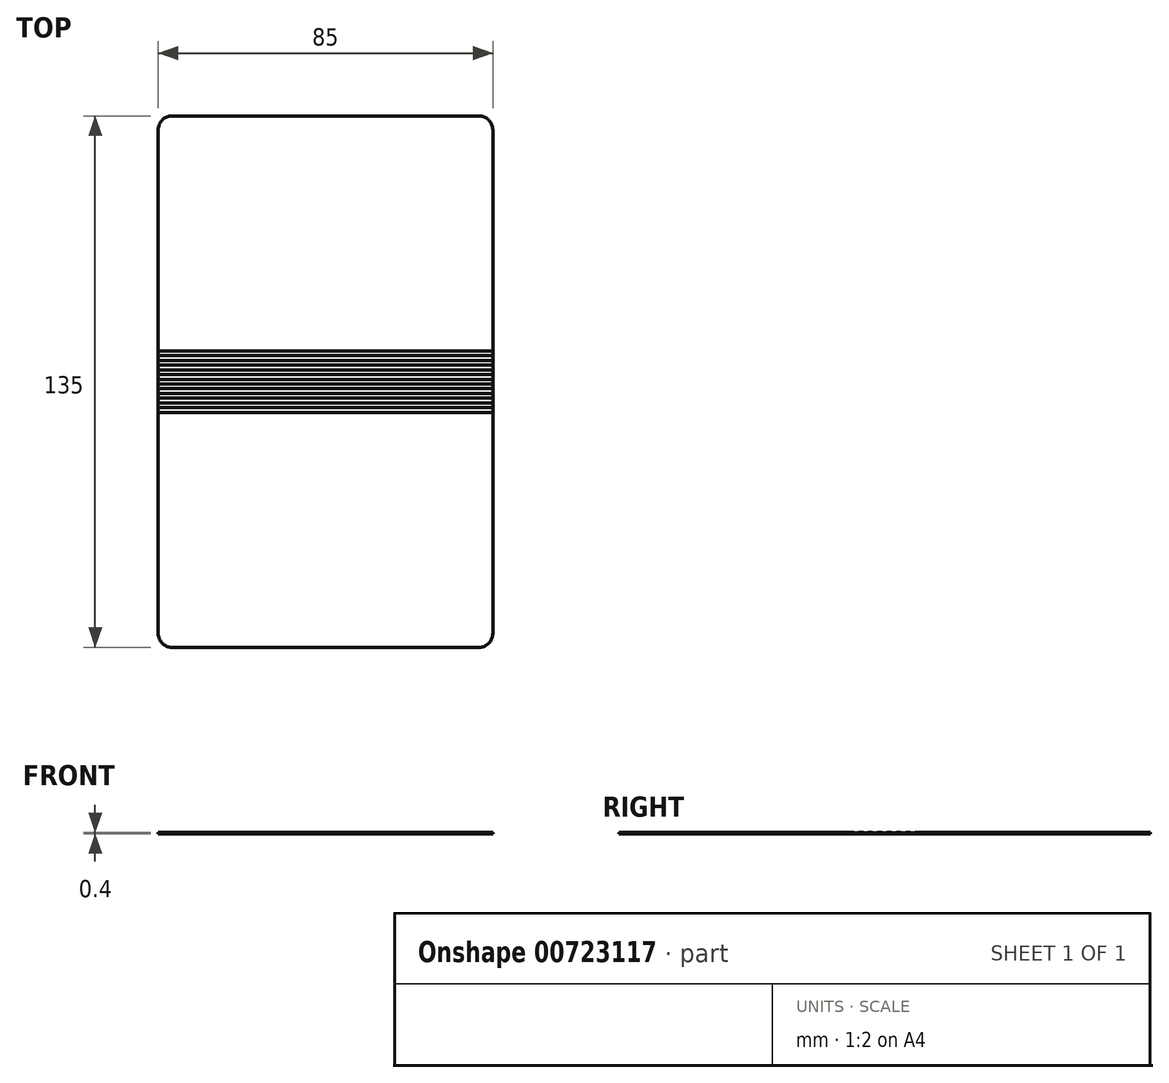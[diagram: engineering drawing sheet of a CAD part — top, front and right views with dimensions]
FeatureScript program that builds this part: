
annotation { "Feature Type Name" : "Feature", "Feature Type Description" : "" }
export const myFeature = defineFeature(function(context is Context, id is Id, definition is map)
    precondition{}
    {
        {
            var Q0;
            Q0=qCreatedBy(makeId("Top.planeOp"),FACE);
            var sketch = newSketch(context, id + "F0", { "sketchPlane" : qUnion([Q0])});
            skLineSegment(sketch, "E0.bottom", {"start": v(39, 67.5) * mm, "end": v(-39, 67.5) * mm});
            skLineSegment(sketch, "E0.top", {"start": v(39, -67.5) * mm, "end": v(-39, -67.5) * mm});
            skLineSegment(sketch, "E0.left", {"start": v(42.5, 64) * mm, "end": v(42.5, -64) * mm});
            skLineSegment(sketch, "E0.right", {"start": v(-42.5, 64) * mm, "end": v(-42.5, -64) * mm});
            skPoint(sketch, "E0.middle", {"position": v(0, 0) * mm});
            skPoint(sketch, "E1.visualSharp", {"position": v(-42.5, 67.5) * mm});
            skArc(sketch, "E1.filletArc", {"start": v(-39, 67.5) * mm, "mid": v(-41.47, 66.47) * mm, "end": v(-42.5, 64) * mm});
            skPoint(sketch, "E2.visualSharp", {"position": v(42.5, 67.5) * mm});
            skArc(sketch, "E2.filletArc", {"start": v(42.5, 64) * mm, "mid": v(41.47, 66.47) * mm, "end": v(39, 67.5) * mm});
            skPoint(sketch, "E3.visualSharp", {"position": v(42.5, -67.5) * mm});
            skArc(sketch, "E3.filletArc", {"start": v(39, -67.5) * mm, "mid": v(41.47, -66.47) * mm, "end": v(42.5, -64) * mm});
            skPoint(sketch, "E4.visualSharp", {"position": v(-42.5, -67.5) * mm});
            skArc(sketch, "E4.filletArc", {"start": v(-42.5, -64) * mm, "mid": v(-41.47, -66.47) * mm, "end": v(-39, -67.5) * mm});
            skSolve(sketch);
        }
        {
            var Q0;
            Q0=qSketchRegion(id+"F0",true);
            extrude(context, id + "F1", {"entities" : qUnion([Q0]), "depth" : .2 * mm, "offsetDistance" : 25 * mm});
        }
        {
            var Q0;
            Q0=makeQuery(id+"F1.opExtrude","CAP_FACE",FACE,{"disambiguationData":[OSD([sQuery(id+"F0.wireOp",EDGE,"E0.bottom"),sQuery(id+"F0.wireOp",EDGE,"E0.top"),sQuery(id+"F0.wireOp",EDGE,"E0.left"),sQuery(id+"F0.wireOp",EDGE,"E0.right"),sQuery(id+"F0.wireOp",EDGE,"E1.filletArc"),sQuery(id+"F0.wireOp",EDGE,"E2.filletArc"),sQuery(id+"F0.wireOp",EDGE,"E3.filletArc"),sQuery(id+"F0.wireOp",EDGE,"E4.filletArc")])],"isStart":false});
            var sketch = newSketch(context, id + "F2", { "sketchPlane" : qUnion([Q0])});
            skLineSegment(sketch, "E5.0", {"start": v(-42.5, -0.6) * mm, "end": v(42.5, -0.6) * mm});
            skLineSegment(sketch, "E6.0", {"start": v(-42.5, 0.6) * mm, "end": v(42.5, 0.6) * mm});
            skLineSegment(sketch, "E7", {"start": v(-42.5, 0.6) * mm, "end": v(-42.5, -0.6) * mm});
            skLineSegment(sketch, "E8", {"start": v(42.5, 0.6) * mm, "end": v(42.5, -0.6) * mm});
            skLineSegment(sketch, "E9.0.1.0", {"start": v(42.5, 3) * mm, "end": v(42.5, 1.8) * mm});
            skLineSegment(sketch, "E9.0.1.1", {"start": v(-42.5, 3) * mm, "end": v(42.5, 3) * mm});
            skLineSegment(sketch, "E9.0.1.2", {"start": v(-42.5, 1.8) * mm, "end": v(42.5, 1.8) * mm});
            skLineSegment(sketch, "E9.0.1.3", {"start": v(-42.5, 3) * mm, "end": v(-42.5, 1.8) * mm});
            skLineSegment(sketch, "E9.0.2.0", {"start": v(42.5, 5.4) * mm, "end": v(42.5, 4.2) * mm});
            skLineSegment(sketch, "E9.0.2.1", {"start": v(-42.5, 5.4) * mm, "end": v(42.5, 5.4) * mm});
            skLineSegment(sketch, "E9.0.2.2", {"start": v(-42.5, 4.2) * mm, "end": v(42.5, 4.2) * mm});
            skLineSegment(sketch, "E9.0.2.3", {"start": v(-42.5, 5.4) * mm, "end": v(-42.5, 4.2) * mm});
            skLineSegment(sketch, "E9.direction1", {"start": v(42.5, -0.6) * mm, "end": v(67.5, -0.6) * mm, "construction": true});
            skLineSegment(sketch, "E9.direction2", {"start": v(42.5, -0.6) * mm, "end": v(42.5, 1.8) * mm, "construction": true});
            skLineSegment(sketch, "E10.MirrorCS", {"start": v(-42.5, -1.8) * mm, "end": v(42.5, -1.8) * mm});
            skLineSegment(sketch, "E11.MirrorCS", {"start": v(42.5, -3) * mm, "end": v(42.5, -1.8) * mm});
            skLineSegment(sketch, "E12.MirrorCS", {"start": v(-42.5, -3) * mm, "end": v(42.5, -3) * mm});
            skLineSegment(sketch, "E13.MirrorCS", {"start": v(-42.5, -4.2) * mm, "end": v(42.5, -4.2) * mm});
            skLineSegment(sketch, "E14.MirrorCS", {"start": v(42.5, -5.4) * mm, "end": v(42.5, -4.2) * mm});
            skLineSegment(sketch, "E15.MirrorCS", {"start": v(-42.5, -5.4) * mm, "end": v(42.5, -5.4) * mm});
            skLineSegment(sketch, "E16.MirrorCS", {"start": v(-42.5, -5.4) * mm, "end": v(-42.5, -4.2) * mm});
            skLineSegment(sketch, "E17.MirrorCS", {"start": v(-42.5, -3) * mm, "end": v(-42.5, -1.8) * mm});
            skLineSegment(sketch, "E18.0.0.3", {"start": v(42.5, 7.8) * mm, "end": v(42.5, 6.6) * mm});
            skLineSegment(sketch, "E18.3.0.3", {"start": v(-42.5, 7.8) * mm, "end": v(42.5, 7.8) * mm});
            skLineSegment(sketch, "E18.6.0.3", {"start": v(-42.5, 6.6) * mm, "end": v(42.5, 6.6) * mm});
            skLineSegment(sketch, "E18.9.0.3", {"start": v(-42.5, 7.8) * mm, "end": v(-42.5, 6.6) * mm});
            skLineSegment(sketch, "E19.MirrorCS", {"start": v(42.5, -7.8) * mm, "end": v(42.5, -6.6) * mm});
            skLineSegment(sketch, "E20.MirrorCS", {"start": v(-42.5, -6.6) * mm, "end": v(42.5, -6.6) * mm});
            skLineSegment(sketch, "E21.MirrorCS", {"start": v(-42.5, -7.8) * mm, "end": v(42.5, -7.8) * mm});
            skLineSegment(sketch, "E22.MirrorCS", {"start": v(-42.5, -7.8) * mm, "end": v(-42.5, -6.6) * mm});
            skSolve(sketch);
        }
        {
            var Q0;
            Q0=qSketchRegion(id+"F0",true);
            extrude(context, id + "F3", {"entities" : qUnion([Q0]), "operationType" : NewBodyOperationType.ADD, "depth" : .4 * mm, "offsetDistance" : 25 * mm});
        }
        {
            var Q0;
            Q0=qSketchRegion(id+"F2",true);
            var Q1;
            Q1=makeQuery(id+"F3.opExtrude","CAP_FACE",FACE,{"disambiguationData":[OSD([sQuery(id+"F0.wireOp",EDGE,"E0.bottom"),sQuery(id+"F0.wireOp",EDGE,"E0.top"),sQuery(id+"F0.wireOp",EDGE,"E0.left"),sQuery(id+"F0.wireOp",EDGE,"E0.right"),sQuery(id+"F0.wireOp",EDGE,"E1.filletArc"),sQuery(id+"F0.wireOp",EDGE,"E2.filletArc"),sQuery(id+"F0.wireOp",EDGE,"E3.filletArc"),sQuery(id+"F0.wireOp",EDGE,"E4.filletArc")])],"isStart":false});
            extrude(context, id + "F4", {"entities" : qUnion([Q0]), "operationType" : NewBodyOperationType.REMOVE, "endBound" : BoundingType.UP_TO_SURFACE, "depth" : 25 * mm, "endBoundEntityFace" : qUnion([Q1]), "offsetDistance" : 25 * mm});
        }
    });
